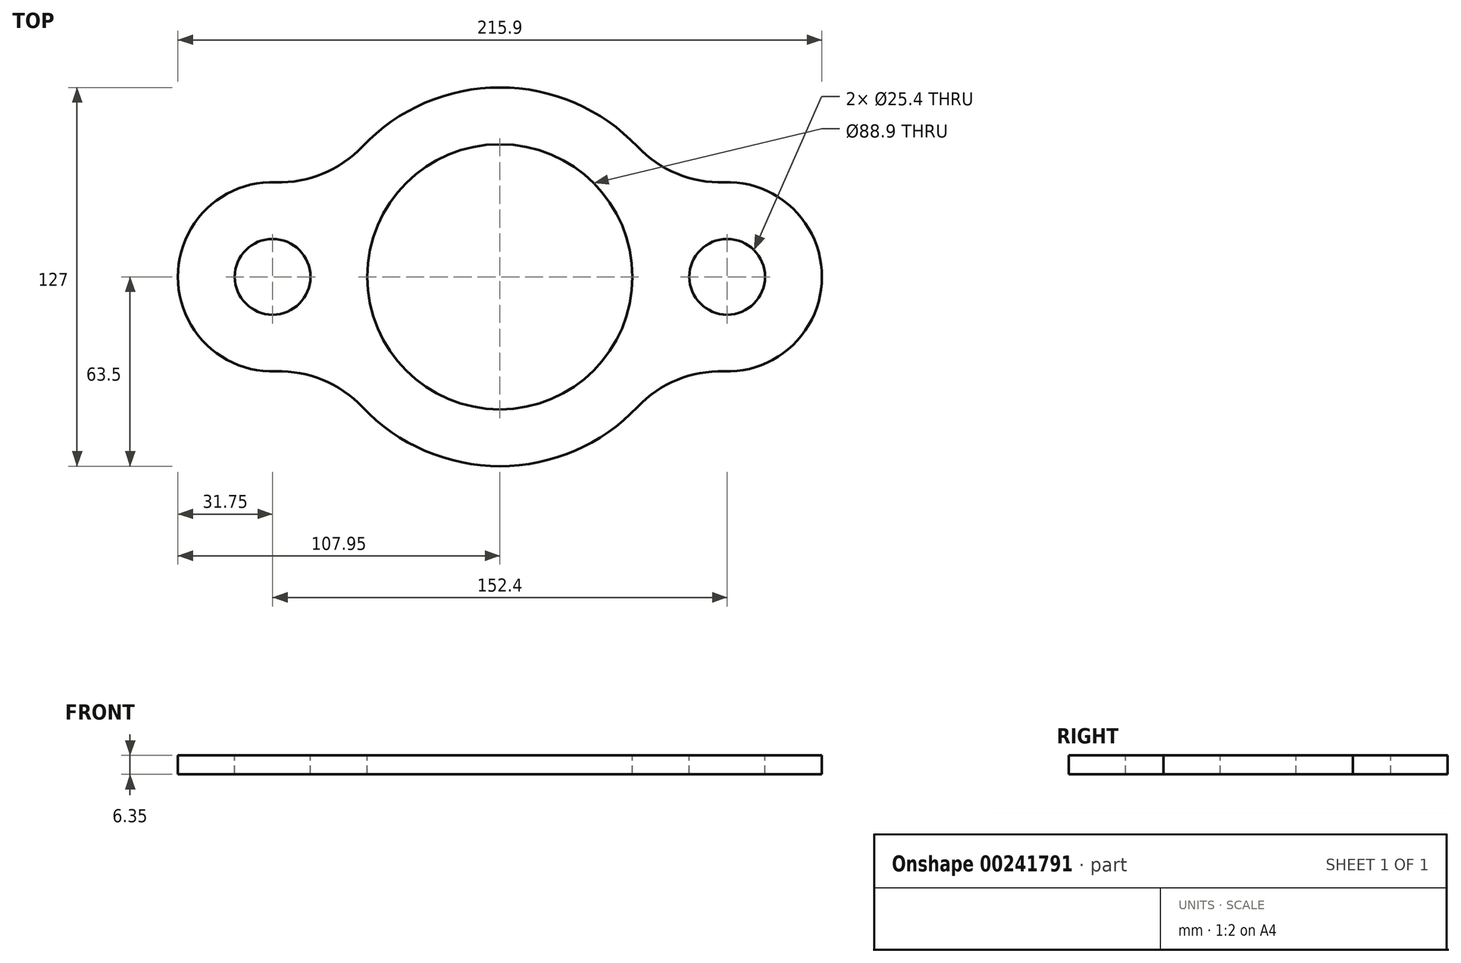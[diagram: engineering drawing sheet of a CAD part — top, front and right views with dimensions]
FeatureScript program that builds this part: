
annotation { "Feature Type Name" : "Feature", "Feature Type Description" : "" }
export const myFeature = defineFeature(function(context is Context, id is Id, definition is map)
    precondition{}
    {
        {
            var Q0;
            Q0=qCreatedBy(makeId("Top.planeOp"),FACE);
            var sketch = newSketch(context, id + "F0", { "sketchPlane" : qUnion([Q0])});
            skCircle(sketch, "E0", {"center": v(0, 0) * mm, "radius": 44.45 * mm});
            skCircle(sketch, "E1", {"center": v(-76.2, 0) * mm, "radius": 12.7 * mm});
            skArc(sketch, "E2", {"start": v(-75.12, 31.73) * mm, "mid": v(-107.95, 0) * mm, "end": v(-75.12, -31.73) * mm});
            skArc(sketch, "E3", {"start": v(75.12, -31.73) * mm, "mid": v(107.95, 0) * mm, "end": v(75.12, 31.73) * mm});
            skArc(sketch, "E4", {"start": v(-46.14, -43.63) * mm, "mid": v(0, -63.5) * mm, "end": v(46.14, -43.63) * mm});
            skArc(sketch, "E5.trimOffspring", {"start": v(46.14, 43.63) * mm, "mid": v(0, 63.5) * mm, "end": v(-46.14, 43.63) * mm});
            skPoint(sketch, "E6.visualSharp", {"position": v(-57.94, 25.98) * mm});
            skArc(sketch, "E6.filletArc", {"start": v(-75.12, 31.73) * mm, "mid": v(-59.35, 34.56) * mm, "end": v(-46.14, 43.63) * mm});
            skPoint(sketch, "E7.visualSharp", {"position": v(57.94, 25.98) * mm});
            skArc(sketch, "E7.filletArc", {"start": v(46.14, 43.63) * mm, "mid": v(59.35, 34.56) * mm, "end": v(75.12, 31.73) * mm});
            skPoint(sketch, "E8.visualSharp", {"position": v(57.94, -25.98) * mm});
            skArc(sketch, "E8.filletArc", {"start": v(75.12, -31.73) * mm, "mid": v(59.35, -34.56) * mm, "end": v(46.14, -43.63) * mm});
            skPoint(sketch, "E9.visualSharp", {"position": v(-57.94, -25.98) * mm});
            skArc(sketch, "E9.filletArc", {"start": v(-46.14, -43.63) * mm, "mid": v(-59.35, -34.56) * mm, "end": v(-75.12, -31.73) * mm});
            skCircle(sketch, "E10", {"center": v(76.2, 0) * mm, "radius": 12.7 * mm});
            skSolve(sketch);
        }
        {
            var Q0;
            Q0 = qSketchRegion(id + "F0", true);
            extrude(context, id + "F1", {"entities" : qUnion([Q0]), "oppositeDirection" : true, "depth" : 6.35 * mm});
        }
    });
